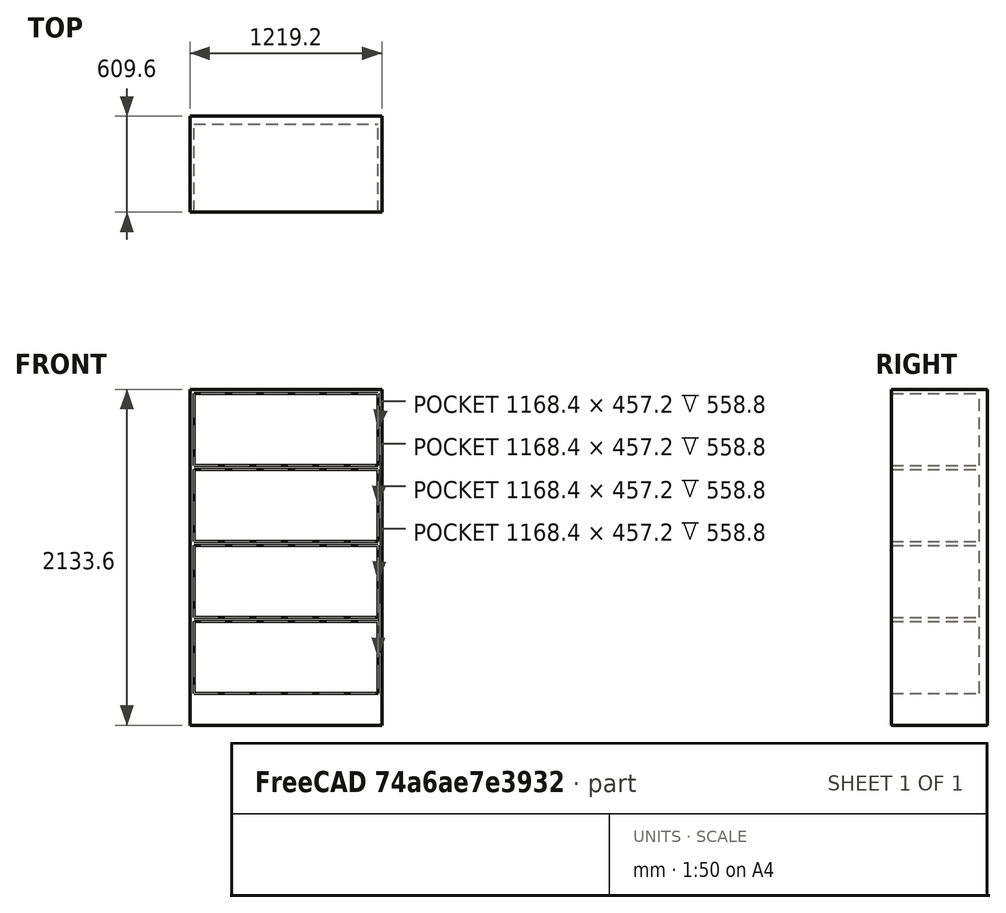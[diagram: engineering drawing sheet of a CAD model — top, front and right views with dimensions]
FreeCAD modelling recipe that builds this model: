
FCSTD DOCUMENT  (FreeCAD 0.17R7668 (Git))
Label: Generic - Open cabinet
License: All rights reserved
LicenseURL: http://en.wikipedia.org/wiki/All_rights_reserved
objects: Part::Box×5, Part::Cut×4
note: 9 computed .brp shape members not serialized (recipe doc carries the construction recipe); baked Part::Feature solids carry a one-line shape summary decoded from their .brp

FEATURE [Part::Box] Box  label="Cube"
  AttacherType = Attacher::AttachEngine3D
  Height = 2133.6
  Length = 1219.2
  Width = 609.6
FEATURE [Part::Box] Box001  label="Cube001"
  AttacherType = Attacher::AttachEngine3D
  Height = 457.2
  Length = 1168.4
  Placement = pos=(25.4,0,1168.4) rot=(0,0,1;0rad)
  Width = 558.8
FEATURE [Part::Cut] Cut
  Base = -> Box
  Tool = -> Box001
FEATURE [Part::Box] Box002  label="Cube002"
  AttacherType = Attacher::AttachEngine3D
  Height = 457.2
  Length = 1168.4
  Placement = pos=(25.4,0,203.2) rot=(0,0,1;0rad)
  Width = 558.8
FEATURE [Part::Box] Box003  label="Cube003"
  AttacherType = Attacher::AttachEngine3D
  Height = 457.2
  Length = 1168.4
  Placement = pos=(25.4,0,685.8) rot=(0,0,1;0rad)
  Width = 558.8
FEATURE [Part::Box] Box004  label="Cube004"
  AttacherType = Attacher::AttachEngine3D
  Height = 457.2
  Length = 1168.4
  Placement = pos=(25.4,0,1651) rot=(0,0,1;0rad)
  Width = 558.8
FEATURE [Part::Cut] Cut001
  Base = -> Cut
  Tool = -> Box002
FEATURE [Part::Cut] Cut002
  Base = -> Cut001
  Tool = -> Box003
FEATURE [Part::Cut] Cut003
  Base = -> Cut002
  Tool = -> Box004
